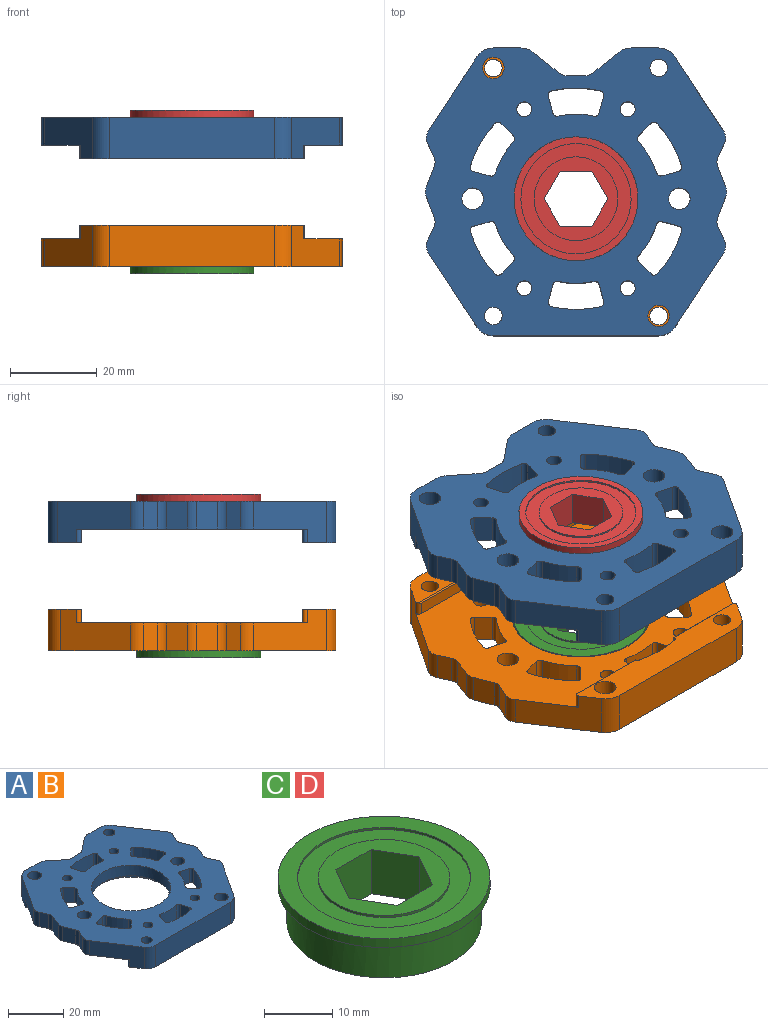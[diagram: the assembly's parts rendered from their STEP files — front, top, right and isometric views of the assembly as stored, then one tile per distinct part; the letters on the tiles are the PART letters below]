
ASSEMBLY  parts=4 mates=4
PART A: 111 faces, bbox 69.4x66.3x9.5 mm
  f0: cylinder r=15.88mm len=31.75mm, axis (0,0,-1), area 164.7mm2, adj f97,f110
  f1: cylinder r=2.54mm len=6.35mm, axis (0,0,1), area 12.9mm2, adj f35,f36,f50,f97
  f2: cylinder r=2.54mm len=6.35mm, axis (0,0,-1), area 12.9mm2, adj f44,f45,f50,f97
  f3: cylinder r=2.49mm len=6.35mm, axis (0,0,1), area 99.3mm2, adj f50,f97
  f4: cylinder r=2.49mm len=6.35mm, axis (0,0,1), area 99.3mm2, adj f50,f97
  f5: cylinder r=0.79mm len=3.18mm, axis (0,0,1), area 5.3mm2, adj f25,f43,f96,f97,f102
  f6: cylinder r=0.79mm len=3.18mm, axis (0,0,-1), area 5.3mm2, adj f25,f39,f95,f97,f101
  f7: cylinder r=2.02mm len=9.53mm, axis (0,0,1), area 120.8mm2, adj f50,f51
  f8: cylinder r=2.02mm len=9.53mm, axis (0,0,1), area 120.8mm2, adj f25,f50
  f9: cylinder r=3.17mm len=6.35mm, axis (0,0,-1), area 14.8mm2, adj f36,f37,f50,f97
  f10: cylinder r=3.17mm len=6.35mm, axis (0,0,1), area 20.5mm2, adj f47,f48,f50,f97
  f11: cylinder r=3.17mm len=6.35mm, axis (0,0,1), area 20.4mm2, adj f43,f44,f50,f97
  f12: cylinder r=1mm len=6.35mm, axis (0,0,1), area 9.7mm2, adj f50,f87,f93,f97
  f13: cylinder r=1mm len=9.53mm, axis (0,0,1), area 14.5mm2, adj f25,f50,f82,f83,f96,f97,f102
  f14: cylinder r=1mm len=6.35mm, axis (0,0,1), area 10.2mm2, adj f50,f73,f79,f97
  f15: cylinder r=1mm len=6.35mm, axis (0,0,1), area 10.2mm2, adj f50,f66,f67,f97
  f16: cylinder r=1mm len=6.35mm, axis (0,0,1), area 10.2mm2, adj f50,f59,f60,f97
  f17: cylinder r=1mm len=6.35mm, axis (0,0,1), area 9.7mm2, adj f50,f52,f58,f97
  f18: cylinder r=1.73mm len=6.35mm, axis (0,0,1), area 68.9mm2, adj f50,f97
  f19: cylinder r=1.73mm len=6.35mm, axis (0,0,1), area 68.9mm2, adj f50,f97
  f20: cylinder r=1.73mm len=6.35mm, axis (0,0,1), area 68.9mm2, adj f50,f97
  f21: cylinder r=1.73mm len=6.35mm, axis (0,0,1), area 68.9mm2, adj f50,f97
  f22: cylinder r=2.49mm len=9.53mm, axis (0,0,-1), area 149mm2, adj f50,f51
  f23: cylinder r=2.49mm len=9.53mm, axis (0,0,-1), area 149mm2, adj f25,f50
  f24: cylinder r=14.27mm len=28.55mm, axis (0,0,-1), area 421.5mm2, adj f50,f110
  f25: plane 51.79x7.45mm, normal (0,0,-1), area 308.4mm2, adj f5,f6,f8,f13,f23,f39,f40,f41
  f26: plane 9.53x6.35mm, normal (0,1,0), area 60.5mm2, adj f27,f49,f50,f51
  f27: cylinder r=4.58mm len=9.53mm, axis (0,0,-1), area 29.5mm2, adj f26,f28,f50,f51
  f28: plane 9.53x5.96mm, normal (-0.63,0.78,0), area 72.8mm2, adj f27,f50,f51,f106
  f29: plane 9.53x4.56mm, normal (0,1,0), area 43.5mm2, adj f50,f51,f106,f107
  f30: plane 9.53x5.96mm, normal (0.63,0.78,0), area 72.8mm2, adj f31,f50,f51,f107
  f31: cylinder r=4.58mm len=9.53mm, axis (0,0,-1), area 29.5mm2, adj f30,f32,f50,f51
  f32: plane 9.53x6.35mm, normal (0,1,0), area 60.5mm2, adj f31,f33,f50,f51
  f33: cylinder r=4.58mm len=9.53mm, axis (0,0,-1), area 43.3mm2, adj f32,f34,f50,f51
  f34: plane 16.91x11.08mm, normal (-0.84,0.55,0), area 145.1mm2, adj f33,f50,f51,f97,f99,f104
  f35: plane 6.35x3.19mm, normal (-0.91,-0.42,0), area 22.3mm2, adj f1,f50,f97,f99
  f36: plane 6.35x4.8mm, normal (-0.93,0.36,0), area 32.6mm2, adj f1,f9,f50,f97
  f37: plane 6.35x4.8mm, normal (-0.93,-0.36,0), area 32.6mm2, adj f9,f50,f97,f109
  f38: plane 6.35x3.19mm, normal (-0.91,0.42,0), area 22.3mm2, adj f50,f97,f98,f109
  f39: plane 16.91x11.08mm, normal (-0.84,-0.55,0), area 145.1mm2, adj f6,f25,f40,f50,f97,f98
  f40: cylinder r=4.58mm len=9.53mm, axis (0,0,-1), area 43.3mm2, adj f25,f39,f41,f50
  f41: plane 38.1x9.53mm, normal (0,-1,0), area 362.9mm2, adj f25,f40,f42,f50
  f42: cylinder r=4.58mm len=9.53mm, axis (0,0,-1), area 43.3mm2, adj f25,f41,f43,f50
  f43: plane 16.91x11.08mm, normal (0.84,-0.55,0), area 145.1mm2, adj f5,f11,f25,f42,f50,f97
  f44: plane 6.35x3.19mm, normal (0.91,0.42,0), area 22.3mm2, adj f2,f11,f50,f97
  f45: plane 6.35x4.8mm, normal (0.93,-0.36,0), area 32.6mm2, adj f2,f50,f97,f100
  f46: plane 6.35x4.8mm, normal (0.93,0.36,0), area 32.6mm2, adj f50,f97,f100,f108
  f47: plane 6.35x3.19mm, normal (0.91,-0.42,0), area 22.3mm2, adj f10,f50,f97,f108
  f48: plane 16.04x10.62mm, normal (0.83,0.55,0), area 135.6mm2, adj f10,f49,f50,f51,f97,f105
  f49: cylinder r=4.58mm len=9.53mm, axis (0,0,-1), area 52.6mm2, adj f26,f48,f50,f51
  f50: plane 69.4x66.32mm, normal (0,0,1), area 2716.2mm2, adj f1,f2,f3,f4,f7,f8,f9,f10
  f51: plane 51.69x7.45mm, normal (0,0,-1), area 230.8mm2, adj f7,f22,f26,f27,f28,f29,f30,f31
  f52: cylinder r=19.5mm len=7.2mm, axis (0,0,1), area 53.2mm2, adj f17,f50,f53,f97
  f53: cylinder r=1mm len=6.35mm, axis (0,0,1), area 9.7mm2, adj f50,f52,f54,f97
  f54: plane 6.35x3.87mm, normal (0.26,0.97,0), area 25.4mm2, adj f50,f53,f55,f97
  f55: cylinder r=1mm len=6.35mm, axis (0,0,1), area 10.2mm2, adj f50,f54,f56,f97
  f56: cylinder r=25.5mm len=9.75mm, axis (0,0,1), area 72.1mm2, adj f50,f55,f57,f97
  f57: cylinder r=1mm len=6.35mm, axis (0,0,1), area 10.2mm2, adj f50,f56,f58,f97
  f58: plane 6.35x2.83mm, normal (-0.71,-0.71,0), area 25.4mm2, adj f17,f50,f57,f97
  f59: cylinder r=25.5mm len=11.26mm, axis (0,0,1), area 72.1mm2, adj f16,f50,f65,f97
  f60: plane 6.35x3.87mm, normal (-0.97,0.26,0), area 25.4mm2, adj f16,f50,f61,f97
  f61: cylinder r=1mm len=6.35mm, axis (0,0,1), area 9.7mm2, adj f50,f60,f62,f97
  f62: cylinder r=19.5mm len=8.32mm, axis (0,0,1), area 53.2mm2, adj f50,f61,f63,f97
  f63: cylinder r=1mm len=6.35mm, axis (0,0,1), area 9.7mm2, adj f50,f62,f64,f97
  f64: plane 6.35x3.87mm, normal (0.97,0.26,0), area 25.4mm2, adj f50,f63,f65,f97
  f65: cylinder r=1mm len=6.35mm, axis (0,0,1), area 10.2mm2, adj f50,f59,f64,f97
  f66: cylinder r=25.5mm len=9.74mm, axis (0,0,1), area 72.1mm2, adj f15,f50,f72,f97
  f67: plane 6.35x3.87mm, normal (-0.26,0.97,0), area 25.4mm2, adj f15,f50,f68,f97
  f68: cylinder r=1mm len=6.35mm, axis (0,0,1), area 9.7mm2, adj f50,f67,f69,f97
  f69: cylinder r=19.5mm len=7.2mm, axis (0,0,1), area 53.2mm2, adj f50,f68,f70,f97
  f70: cylinder r=1mm len=6.35mm, axis (0,0,1), area 9.7mm2, adj f50,f69,f71,f97
  f71: plane 6.35x2.83mm, normal (0.71,-0.71,0), area 25.4mm2, adj f50,f70,f72,f97
  f72: cylinder r=1mm len=6.35mm, axis (0,0,1), area 10.2mm2, adj f50,f66,f71,f97
  f73: cylinder r=25.5mm len=9.75mm, axis (0,0,1), area 72.1mm2, adj f14,f50,f74,f97
  f74: cylinder r=1mm len=6.35mm, axis (0,0,1), area 10.2mm2, adj f50,f73,f75,f97
  f75: plane 6.35x2.83mm, normal (0.71,0.71,0), area 25.4mm2, adj f50,f74,f76,f97
  f76: cylinder r=1mm len=6.35mm, axis (0,0,1), area 9.7mm2, adj f50,f75,f77,f97
  f77: cylinder r=19.5mm len=7.2mm, axis (0,0,1), area 53.2mm2, adj f50,f76,f78,f97
  f78: cylinder r=1mm len=6.35mm, axis (0,0,1), area 9.7mm2, adj f50,f77,f79,f97
  f79: plane 6.35x3.87mm, normal (-0.26,-0.97,0), area 25.4mm2, adj f14,f50,f78,f97
  f80: cylinder r=19.5mm len=8.32mm, axis (0,0,1), area 53.2mm2, adj f50,f81,f86,f97
  f81: cylinder r=1mm len=6.35mm, axis (0,0,1), area 9.7mm2, adj f50,f80,f82,f97
  f82: plane 6.35x3.87mm, normal (-0.97,-0.26,0), area 25.4mm2, adj f13,f50,f81,f97
  f83: cylinder r=25.5mm len=11.26mm, axis (0,0,1), area 108.1mm2, adj f13,f25,f50,f84
  f84: cylinder r=1mm len=9.53mm, axis (0,0,1), area 14.6mm2, adj f25,f50,f83,f85,f95,f97,f101
  f85: plane 6.35x3.87mm, normal (0.97,-0.26,0), area 25.4mm2, adj f50,f84,f86,f97
  f86: cylinder r=1mm len=6.35mm, axis (0,0,1), area 9.7mm2, adj f50,f80,f85,f97
  f87: plane 6.35x2.83mm, normal (-0.71,0.71,0), area 25.4mm2, adj f12,f50,f88,f97
  f88: cylinder r=1mm len=6.35mm, axis (0,0,1), area 10.2mm2, adj f50,f87,f89,f97
  f89: cylinder r=25.5mm len=9.74mm, axis (0,0,1), area 72.1mm2, adj f50,f88,f90,f97
  f90: cylinder r=1mm len=6.35mm, axis (0,0,1), area 10.2mm2, adj f50,f89,f91,f97
  f91: plane 6.35x3.87mm, normal (0.26,-0.97,0), area 25.4mm2, adj f50,f90,f92,f97
  f92: cylinder r=1mm len=6.35mm, axis (0,0,1), area 9.7mm2, adj f50,f91,f93,f97
  f93: cylinder r=19.5mm len=7.2mm, axis (0,0,1), area 53.2mm2, adj f12,f50,f92,f97
  f94: plane 50.1x2.93mm, normal (0,-1,0), area 146.5mm2, adj f97,f103,f104,f105
  f95: plane 18.7x2.93mm, normal (0,1,0), area 54.7mm2, adj f6,f84,f97,f101
  f96: plane 18.68x2.93mm, normal (0,1,0), area 54.6mm2, adj f5,f13,f97,f102
  f97: plane 69.4x53.39mm, normal (0,0,-1), area 2003.2mm2, adj f0,f1,f2,f3,f4,f5,f6,f9
  f98: cylinder r=3.17mm len=6.35mm, axis (0,0,1), area 20.4mm2, adj f38,f39,f50,f97
  f99: cylinder r=3.17mm len=6.35mm, axis (0,0,1), area 20.4mm2, adj f34,f35,f50,f97
  f100: cylinder r=3.17mm len=6.35mm, axis (0,0,-1), area 14.8mm2, adj f45,f46,f50,f97
  f101: plane 19.31x0.25mm, normal (0,0.71,-0.71), area 6.8mm2, adj f6,f25,f84,f95
  f102: plane 19.29x0.25mm, normal (0,0.71,-0.71), area 6.7mm2, adj f5,f13,f25,f96
  f103: plane 51.26x0.25mm, normal (0,-0.71,-0.71), area 18mm2, adj f51,f94,f104,f105
  f104: cylinder r=0.79mm len=3.18mm, axis (0,0,1), area 5.3mm2, adj f34,f51,f94,f97,f103
  f105: cylinder r=0.79mm len=3.18mm, axis (0,0,-1), area 5.3mm2, adj f48,f51,f94,f97,f103
  f106: cylinder r=2.54mm len=9.53mm, axis (0,0,1), area 16.4mm2, adj f28,f29,f50,f51
  f107: cylinder r=2.54mm len=9.53mm, axis (0,0,1), area 16.4mm2, adj f29,f30,f50,f51
  f108: cylinder r=2.54mm len=6.35mm, axis (0,0,1), area 12.9mm2, adj f46,f47,f50,f97
  f109: cylinder r=2.54mm len=6.35mm, axis (0,0,-1), area 12.9mm2, adj f37,f38,f50,f97
  f110: plane 31.75x31.75mm, normal (0,0,-1), area 151.6mm2, adj f0,f24
PART B: same geometry as A
PART C: 21 faces, bbox 31.1x31.1x7.9 mm
  f0: cylinder r=12.7mm len=25.4mm, axis (0,0,1), area 30.4mm2, adj f1,f2
  f1: plane 25.4x25.4mm, normal (0,0,-1), area 214mm2, adj f0,f3
  f2: plane 28.55x28.55mm, normal (0,0,-1), area 133.5mm2, adj f0,f4
  f3: cylinder r=9.65mm len=19.3mm, axis (0,0,1), area 23.1mm2, adj f1,f5
  f4: cylinder r=14.27mm len=28.55mm, axis (0,0,1), area 502.3mm2, adj f2,f6
  f5: plane 19.3x19.3mm, normal (0,0,-1), area 152.6mm2, adj f3,f7,f8,f9,f10,f11,f12
  f6: cone r=14.27mm half-angle=30deg, axis (0,0,-1), area 38.5mm2, adj f4,f14
  f7: plane 7.94x6.36mm, normal (-0.87,-0.5,0), area 58.3mm2, adj f5,f8,f12,f13
  f8: plane 7.94x6.36mm, normal (-0.87,0.5,0), area 58.3mm2, adj f5,f7,f9,f13
  f9: plane 7.94x7.34mm, normal (0,1,0), area 58.3mm2, adj f5,f8,f10,f13
  f10: plane 7.94x6.36mm, normal (0.87,0.5,0), area 58.3mm2, adj f5,f9,f11,f13
  f11: plane 7.94x6.36mm, normal (0.87,-0.5,0), area 58.3mm2, adj f5,f10,f12,f13
  f12: plane 7.94x7.34mm, normal (0,-1,0), area 58.3mm2, adj f5,f7,f11,f13
  f13: plane 19.3x19.3mm, normal (0,0,1), area 152.6mm2, adj f7,f8,f9,f10,f11,f12,f15
  f14: revolved ~28.55x28.55mm, area 46.4mm2, adj f6,f16
  f15: cylinder r=9.65mm len=19.3mm, axis (0,0,1), area 23.1mm2, adj f13,f17
  f16: plane 31.12x31.12mm, normal (0,0,-1), area 120.6mm2, adj f14,f18
  f17: plane 25.4x25.4mm, normal (0,0,1), area 214mm2, adj f15,f19
  f18: cylinder r=15.56mm len=31.12mm, axis (0,0,1), area 155.2mm2, adj f16,f20
  f19: cylinder r=12.7mm len=25.4mm, axis (0,0,1), area 30.4mm2, adj f17,f20
  f20: plane 31.12x31.12mm, normal (0,0,1), area 253.7mm2, adj f18,f19
PART D: same geometry as C
PLACE A t=(-20.2,-68.42,23.36)mm
PLACE B rot(axis=(0,-1,0),180deg) t=(-20.2,-68.42,-1.46)mm
PLACE C rot(axis=(0,0,1),180deg) t=(-20.2,-70.01,-7.88)mm
PLACE D rot(axis=(1,0,0),180deg) t=(-20.2,-70.01,29.77)mm
MATE planar A.f32 <-> B.f32  axis (0,1,0) through (-36.07,-35.26,23.36)mm
MATE fastened C.f0 <-> B.f0  axis (0,0,-1) through (-20.2,-70.01,-1.53)mm
MATE fastened D.f0 <-> A.f0  axis (0,0,1) through (-20.2,-70.01,23.42)mm
MATE planar B.f36 <-> A.f46  axis (0.93,0.36,0) through (13.37,-64.89,-3.05)mm
